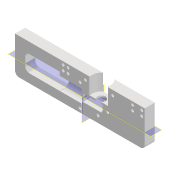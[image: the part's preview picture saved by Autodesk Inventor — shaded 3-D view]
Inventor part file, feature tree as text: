
AUTODESK INVENTOR PART (.ipt)
format: ipt  version: 2022 (Build 260153000, 153)  size: 276,480 bytes
history: native  units: mm
features: reference x17, sketch x11, extrude x10, other x10, plane x6, projected_geometry x4, fillet x3, hole x1
ambient origin geometry x8: Origin, YZ Plane, XZ Plane, XY Plane, X Axis, Y Axis, Z Axis, Center Point
bodies: Solid1 (feature_tree)
feature tree (62):
  extrude  "Extrusion1"  Depth=10.0mm TaperAngle=0.0deg
  fillet  "Fillet1"  Radius=4.0mm
  hole  "Bohrung2"  [1 undecoded]
  extrude  "Extrusion36"  TaperAngle=0.0deg  [1 undecoded]
  extrude  "Extrusion37"  Depth=44.0mm
  plane  "Arbeitsebene10"
  extrude  "Extrusion39"  Depth=4.0mm TaperAngle=0.0deg
  fillet  "Rundung7"  Radius=4.0mm
  sketch  "Skizze43"  dims[d190=0.1mm d191=66.8mm d192=0.0mm]
  plane  "Arbeitsebene11"
  extrude  "Extrusion40"  Depth=0.1mm TaperAngle=0.0deg
  plane  "Arbeitsebene14"
  extrude  "Extrusion41"  Depth=16.0mm TaperAngle=0.0deg
  sketch  "Skizze45"  dims[d197=18.0mm d198=1.0mm d199=10.0mm]
  plane  "Arbeitsebene12"
  extrude  "Extrusion42"  Depth=1.0mm
  fillet  "Rundung8"  Radius=10.0mm
  sketch  "Skizze47"  dims[d204=8.0mm d205=17.0mm d206=0.0mm]
  plane  "Arbeitsebene13"
  extrude  "Extrusion44"  Depth=17.0mm TaperAngle=0.0deg
  sketch  "Skizze48"  dims[d207=0.25mm d208=66.8mm d209=0.0mm]
  plane  "Arbeitsebene15"
  extrude  "Extrusion45"  Depth=66.8mm TaperAngle=0.0deg
  extrude  "Extrusion46"  Depth=0.1mm
  sketch  "Sketch1"  dims[d0=127.8mm d2=10.0mm d3=0.0mm d4=4.0mm]
  sketch  "Skizze38"  dims[d169=2.8mm d170=6.0mm d171=4.0mm d172=2.0mm d173=90.0deg d174=8.0mm d175=20.594885mm d176=0.0mm d177=0.0mm]
  projected_geometry  "Projizierte Kontur16"
  sketch  "Skizze39"  dims[d178=63.9mm d179=0.0mm]
  projected_geometry  "Projizierte Kontur17"
  sketch  "Skizze40"  dims[d180=10.0mm d181=0.0mm d185=44.0mm]
  reference  "Referenz22"
  reference  "Referenz23"
  reference  "Referenz24"
  reference  "Referenz25"
  reference  "Referenz26"
  reference  "Referenz27"
  reference  "Referenz28"
  reference  "Referenz29"
  reference  "Referenz30"
  sketch  "Skizze42"  dims[d186=25.0mm d187=66.8mm d188=0.0mm d189=4.0mm]
  projected_geometry  "Projizierte Kontur18"
  reference  "Referenz33"
  sketch  "Skizze44"  dims[d193=10.0mm d194=0.0mm d195=16.0mm d196=0.0mm]
  reference  "Referenz35"
  projected_geometry  "Projizierte Kontur19"
  reference  "Referenz36"
  reference  "Referenz37"
  reference  "Referenz38"
  sketch  "Skizze49"  dims[d210=10.0mm d211=0.0mm d212=0.1mm]
  reference  "Referenz39"
  reference  "Referenz40"
  reference  "Referenz41"
  other  "<userpath>\Documents\GitHub\Guinardia\INVENTOR\Assembly_HoLiSheet_TwoHalf_v1.iam"
  other  "Assembly_HoLiSheet_TwoHalf_v1.iam"
  other  "10_Wellplate_base_p1_v1:1"
  other  "<userpath>\Documents\GitHub\Guinardia\INVENTOR\Assembly_HoLiSheet_v1.iam"
  other  "Assembly_HoLiSheet_v1.iam"
  other  "00_huawei_p30_Objectivelensassembly:1"
  other  "00_CCTV_lens_M12_25mm_5mp:1"
  other  "20_SMAConnector_fiber:1"
  other  "Assembly_Huawei_P30_Scanninglens:1"
  other  "00_Huawei_P30_Lens_Adapterpcb:1"
note: 2 required parameter values undecoded (feature->parameter linkage not recoverable at this tier; creation-order binding heuristic only, values carry confidence <= 0.55)
